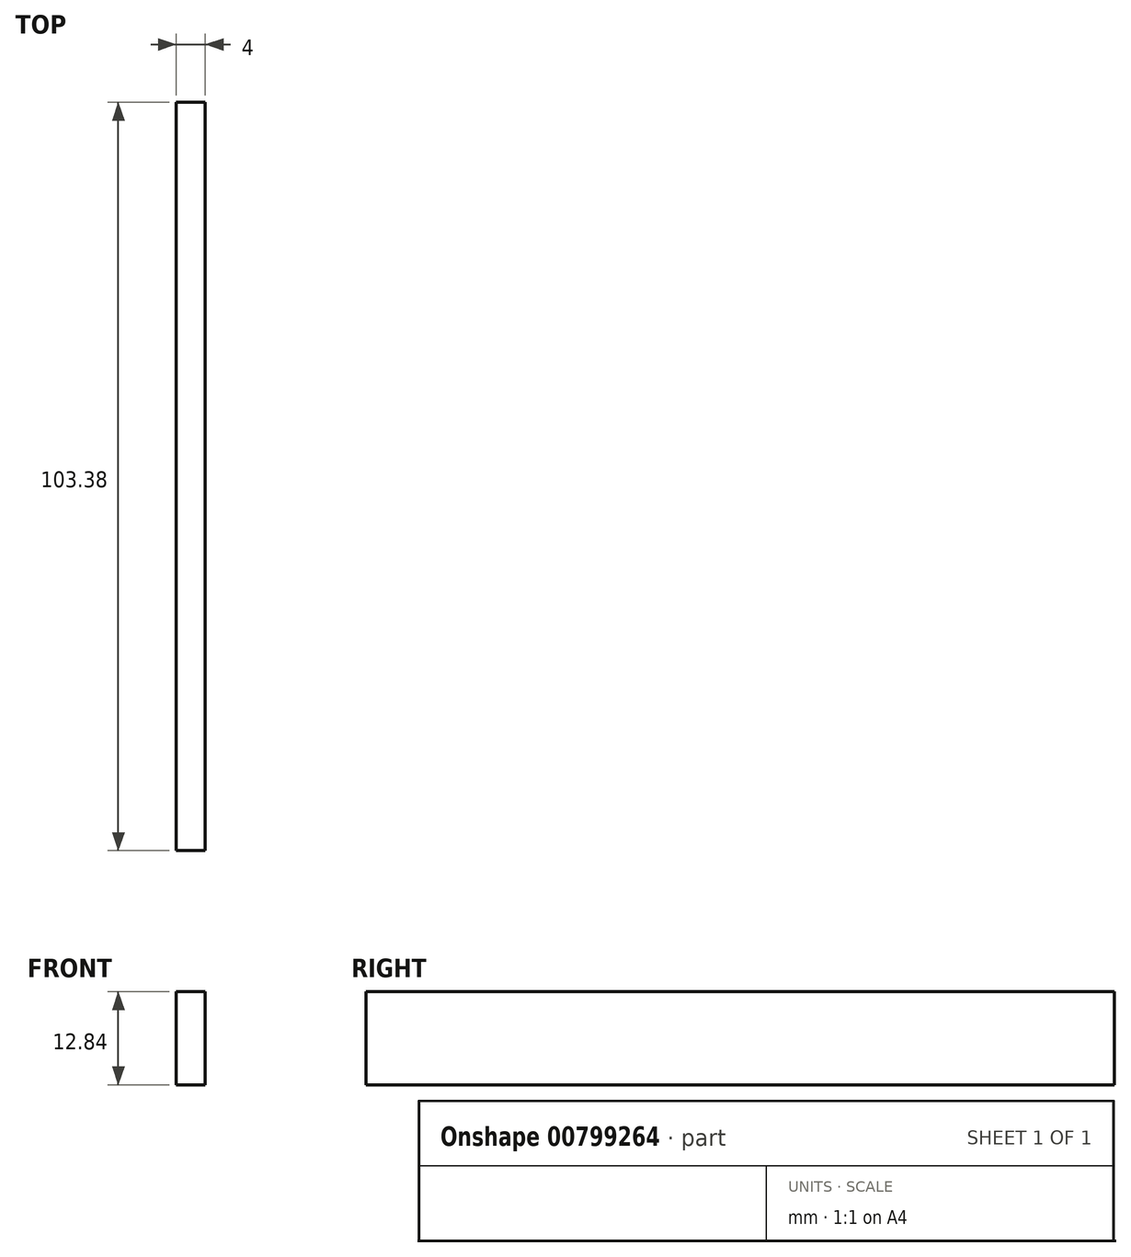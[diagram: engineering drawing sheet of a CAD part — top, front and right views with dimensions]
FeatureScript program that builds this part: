
annotation { "Feature Type Name" : "Feature", "Feature Type Description" : "" }
export const myFeature = defineFeature(function(context is Context, id is Id, definition is map)
    precondition{}
    {
        {
            var Q0;
            Q0=qCreatedBy(makeId("Right.planeOp"),FACE);
            var sketch = newSketch(context, id + "F0", { "sketchPlane" : qUnion([Q0])});
            skLineSegment(sketch, "E0.bottom", {"start": v(-51.7, 6.42) * mm, "end": v(51.7, 6.42) * mm});
            skLineSegment(sketch, "E0.top", {"start": v(-51.7, -6.42) * mm, "end": v(51.7, -6.42) * mm});
            skLineSegment(sketch, "E0.left", {"start": v(-51.7, 6.42) * mm, "end": v(-51.7, -6.42) * mm});
            skLineSegment(sketch, "E0.right", {"start": v(51.7, 6.42) * mm, "end": v(51.7, -6.42) * mm});
            skPoint(sketch, "E0.middle", {"position": v(0, 0) * mm});
            skSolve(sketch);
        }
        {
            var Q0;
            Q0 = qSketchRegion(id + "F0", true);
            extrude(context, id + "F1", {"entities" : qUnion([Q0]), "depth" : 4 * mm, "offsetDistance" : 25 * mm});
        }
    });
